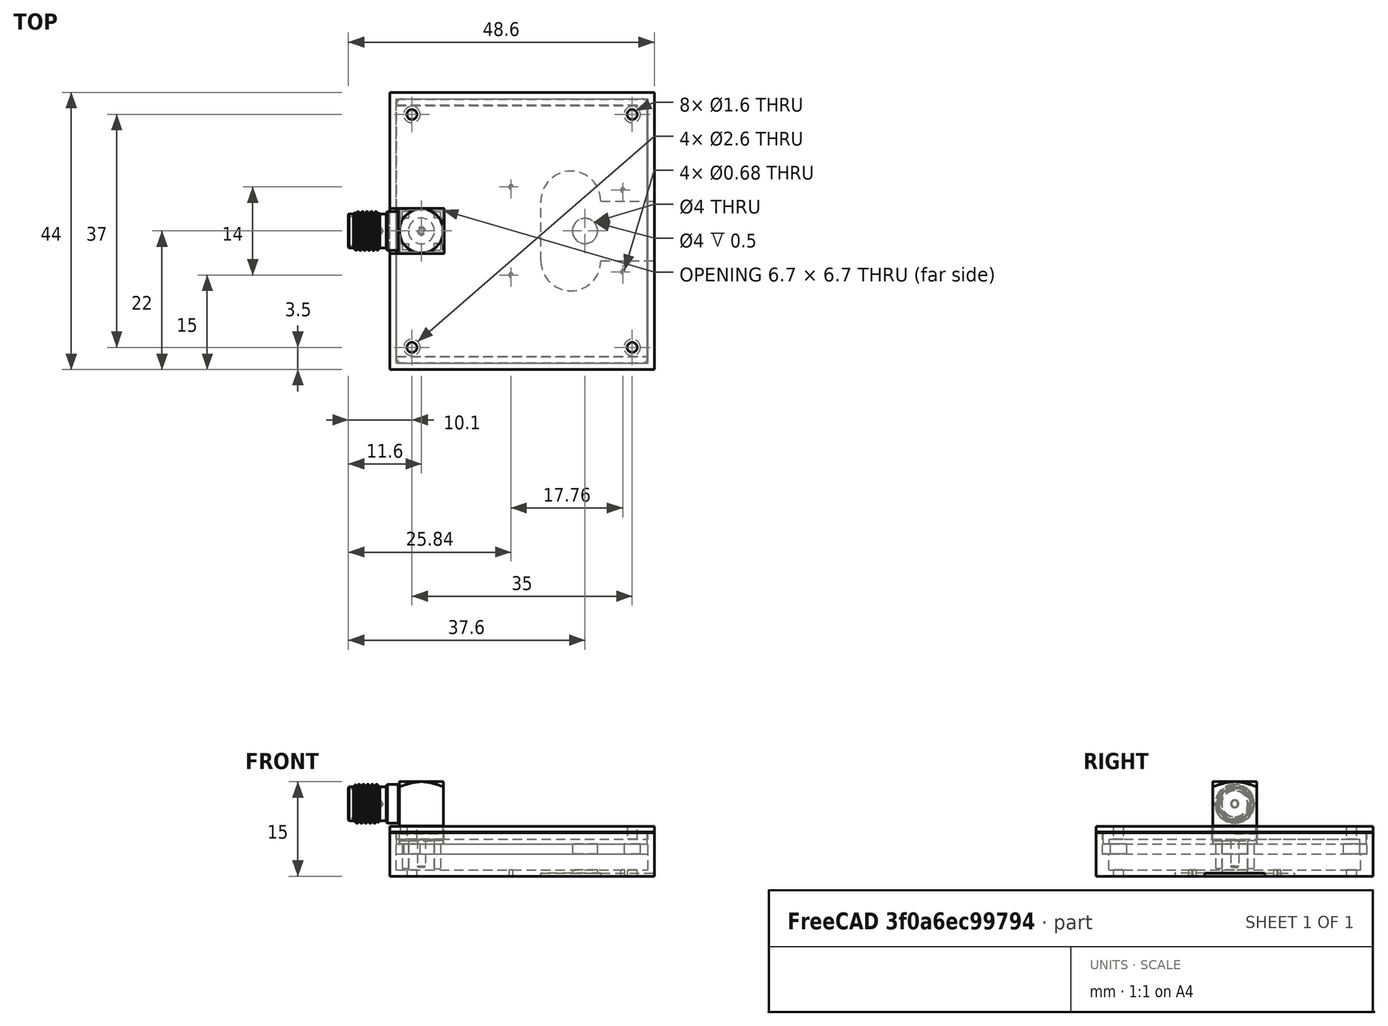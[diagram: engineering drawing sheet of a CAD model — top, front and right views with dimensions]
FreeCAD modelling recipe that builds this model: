
FCSTD DOCUMENT  (FreeCAD 0.20R29603 (Git))
Label: ModulationKickerHousing
License: All rights reserved
LicenseURL: http://en.wikipedia.org/wiki/All_rights_reserved
objects: TechDraw::DrawViewDimension×40, Part::Cylinder×20, Part::Box×11, Part::Cut×9, TechDraw::DrawProjGroupItem×9, Part::Compound×7, Part::MultiFuse×4, TechDraw::DrawSVGTemplate×3, TechDraw::DrawProjGroup×3, TechDraw::DrawPage×3, Part::Feature×1, Part::Fillet×1, TechDraw::DrawViewSection×1
note: 53 computed .brp shape members not serialized (recipe doc carries the construction recipe); baked Part::Feature solids carry a one-line shape summary decoded from their .brp

FEATURE [Part::Box] Box  label="Würfel"
  AttacherType = Attacher::AttachEngine3D
  Height = 1.6
  Length = 40
  Width = 42
FEATURE [Part::Feature] Solid  label="901-143-6RFX"
  Placement = pos=(0,0,0) rot=(1,0,0;-1.5708rad)
  shape: bbox 16.55 x 9.9 x 13.8 mm, 108 faces (baked)
FEATURE [Part::Compound] Compound
  Links = -> [Solid]
  Placement = pos=(4,21,8) rot=(0,0,1;3.14159rad)
FEATURE [Part::Cylinder] Cylinder  label="Zylinder"
  Angle = 360
  AttacherType = Attacher::AttachEngine3D
  FirstAngle = 0
  Height = 5
  Placement = pos=(30,21,0) rot=(0,0,1;0rad)
  Radius = 2
  SecondAngle = 0
FEATURE [Part::Cut] Cut
  Base = -> Box
  Tool = -> Cylinder
FEATURE [Part::Box] Box001  label="Würfel001"
  AttacherType = Attacher::AttachEngine3D
  Height = 7
  Length = 42
  Placement = pos=(-1,-1,-4.4) rot=(0,0,1;0rad)
  Width = 44
FEATURE [Part::Box] Box002  label="Würfel002"
  AttacherType = Attacher::AttachEngine3D
  Height = 6
  Length = 40
  Placement = pos=(0,0,-3.4) rot=(0,0,1;0rad)
  Width = 42
FEATURE [Part::Cut] Cut001
  Base = -> Box001
  Tool = -> Box002
FEATURE [Part::Compound] Compound001  label="PCB"
  Links = -> [Cut,Compound]
  Placement = pos=(0,0,-0.9) rot=(0,0,1;0rad)
FEATURE [Part::Cylinder] Cylinder001  label="Zylinder001"
  Angle = 360
  AttacherType = Attacher::AttachEngine3D
  FirstAngle = 0
  Height = 20
  Placement = pos=(30,21,-10) rot=(0,0,1;0rad)
  Radius = 2
  SecondAngle = 0
FEATURE [Part::Cut] Cut002
  Base = -> Cut001
  Tool = -> Cylinder001
FEATURE [Part::Box] Box003  label="Würfel003"
  AttacherType = Attacher::AttachEngine3D
  Height = 2.5
  Length = 40
  Placement = pos=(0,0,-3.4) rot=(0,0,1;0rad)
  Width = 1
FEATURE [Part::Box] Box004  label="Würfel004"
  AttacherType = Attacher::AttachEngine3D
  Height = 2.5
  Length = 40
  Placement = pos=(0,41,-3.4) rot=(0,0,1;0rad)
  Width = 1
FEATURE [Part::MultiFuse] Fusion
  Shapes = -> [Box003,Box004,Cut002]
FEATURE [Part::Fillet] Fillet  label="PCBRound"
  Base = -> Compound001
  Edges = 4 edges r=1: [Edge1,Edge3,Edge6,Edge12]
FEATURE [Part::Box] Box005  label="Würfel005"
  AttacherType = Attacher::AttachEngine3D
  Height = 1
  Length = 39.8
  Placement = pos=(0.1,0.1,1.5) rot=(0,0,1;0rad)
  Width = 41.8
FEATURE [Part::Box] Box006  label="Würfel006"
  AttacherType = Attacher::AttachEngine3D
  Height = 1
  Length = 42
  Placement = pos=(-1,-1,2.5) rot=(0,0,1;0rad)
  Width = 44
FEATURE [Part::MultiFuse] Fusion001
  Shapes = -> [Box005,Box006]
FEATURE [Part::Box] Box007  label="Würfel007"
  AttacherType = Attacher::AttachEngine3D
  Height = 10
  Length = 20
  Placement = pos=(-12.4,17.4,0) rot=(0,0,1;0rad)
  Width = 7.2
FEATURE [Part::Cut] Cut003
  Base = -> Fusion001
  Tool = -> Box007
FEATURE [Part::Box] Box008  label="Würfel008"
  AttacherType = Attacher::AttachEngine3D
  Height = 0.5
  Length = 18
  Placement = pos=(23,16.25,-4.4) rot=(0,0,1;0rad)
  Width = 9.5
FEATURE [Part::Cylinder] Cylinder002  label="Zylinder002"
  Angle = 360
  AttacherType = Attacher::AttachEngine3D
  FirstAngle = 0
  Height = 0.5
  Placement = pos=(27.75,25.75,-4.4) rot=(0,0,1;0rad)
  Radius = 4.75
  SecondAngle = 0
FEATURE [Part::Cylinder] Cylinder003  label="Zylinder003"
  Angle = 360
  AttacherType = Attacher::AttachEngine3D
  FirstAngle = 0
  Height = 0.5
  Placement = pos=(27.75,16.25,-4.4) rot=(0,0,1;0rad)
  Radius = 4.75
  SecondAngle = 0
FEATURE [Part::MultiFuse] Fusion002
  Shapes = -> [Box008,Cylinder002,Cylinder003]
FEATURE [Part::Cut] Cut004
  Base = -> Fusion
  Tool = -> Fusion002
FEATURE [Part::Cylinder] Cylinder004  label="Zylinder004"
  Angle = 360
  AttacherType = Attacher::AttachEngine3D
  FirstAngle = 0
  Height = 100
  Placement = pos=(18.24,14,-50) rot=(0,0,1;0rad)
  Radius = 0.34
  SecondAngle = 0
FEATURE [Part::Cylinder] Cylinder005  label="Zylinder005"
  Angle = 360
  AttacherType = Attacher::AttachEngine3D
  FirstAngle = 0
  Height = 100
  Placement = pos=(18.24,28,-50) rot=(0,0,1;0rad)
  Radius = 0.34
  SecondAngle = 0
FEATURE [Part::Cylinder] Cylinder006  label="Zylinder006"
  Angle = 360
  AttacherType = Attacher::AttachEngine3D
  FirstAngle = 0
  Height = 100
  Placement = pos=(36,14.5,-50) rot=(0,0,1;0rad)
  Radius = 0.34
  SecondAngle = 0
FEATURE [Part::Cylinder] Cylinder007  label="Zylinder007"
  Angle = 360
  AttacherType = Attacher::AttachEngine3D
  FirstAngle = 0
  Height = 100
  Placement = pos=(36,27.5,-50) rot=(0,0,1;0rad)
  Radius = 0.34
  SecondAngle = 0
FEATURE [Part::Compound] Compound002  label="M1TapHoles"
  Links = -> [Cylinder004,Cylinder005,Cylinder006,Cylinder007]
FEATURE [Part::Cut] Cut005
  Base = -> Cut004
  Tool = -> Compound002
FEATURE [Part::Box] Box009  label="Würfel009"
  AttacherType = Attacher::AttachEngine3D
  Height = 0.8
  Length = 39.8
  Placement = pos=(0.1,40.9,0.7) rot=(0,0,1;0rad)
  Width = 1
FEATURE [Part::Box] Box010  label="Würfel010"
  AttacherType = Attacher::AttachEngine3D
  Height = 0.8
  Length = 39.8
  Placement = pos=(0.1,0.1,0.7) rot=(0,0,1;0rad)
  Width = 1
FEATURE [Part::Compound] Compound003
  Links = -> [Box009,Box010]
FEATURE [Part::MultiFuse] Fusion003
  Shapes = -> [Cut003,Compound003]
FEATURE [Part::Cylinder] Cylinder008  label="Zylinder008"
  Angle = 360
  AttacherType = Attacher::AttachEngine3D
  FirstAngle = 0
  Height = 20
  Placement = pos=(37.5,2.5,-10) rot=(0,0,1;0rad)
  Radius = 0.8
  SecondAngle = 0
FEATURE [Part::Cylinder] Cylinder009  label="Zylinder009"
  Angle = 360
  AttacherType = Attacher::AttachEngine3D
  FirstAngle = 0
  Height = 20
  Placement = pos=(2.5,2.5,-10) rot=(0,0,1;0rad)
  Radius = 0.8
  SecondAngle = 0
FEATURE [Part::Cylinder] Cylinder010  label="Zylinder010"
  Angle = 360
  AttacherType = Attacher::AttachEngine3D
  FirstAngle = 0
  Height = 20
  Placement = pos=(37.5,39.5,-10) rot=(0,0,1;0rad)
  Radius = 0.8
  SecondAngle = 0
FEATURE [Part::Cylinder] Cylinder011  label="Zylinder011"
  Angle = 360
  AttacherType = Attacher::AttachEngine3D
  FirstAngle = 0
  Height = 20
  Placement = pos=(2.5,39.5,-10) rot=(0,0,1;0rad)
  Radius = 0.8
  SecondAngle = 0
FEATURE [Part::Cylinder] Cylinder012  label="Zylinder012"
  Angle = 360
  AttacherType = Attacher::AttachEngine3D
  FirstAngle = 0
  Height = 20
  Placement = pos=(37.5,2.5,-10) rot=(0,0,1;0rad)
  Radius = 1.3
  SecondAngle = 0
FEATURE [Part::Cylinder] Cylinder013  label="Zylinder013"
  Angle = 360
  AttacherType = Attacher::AttachEngine3D
  FirstAngle = 0
  Height = 20
  Placement = pos=(2.5,2.5,-10) rot=(0,0,1;0rad)
  Radius = 1.3
  SecondAngle = 0
FEATURE [Part::Cylinder] Cylinder014  label="Zylinder014"
  Angle = 360
  AttacherType = Attacher::AttachEngine3D
  FirstAngle = 0
  Height = 20
  Placement = pos=(37.5,39.5,-10) rot=(0,0,1;0rad)
  Radius = 1.3
  SecondAngle = 0
FEATURE [Part::Cylinder] Cylinder015  label="Zylinder015"
  Angle = 360
  AttacherType = Attacher::AttachEngine3D
  FirstAngle = 0
  Height = 20
  Placement = pos=(2.5,39.5,-10) rot=(0,0,1;0rad)
  Radius = 1.3
  SecondAngle = 0
FEATURE [Part::Compound] Compound004
  Links = -> [Cylinder015,Cylinder012,Cylinder013,Cylinder014]
FEATURE [Part::Cut] Cut006  label="PCBWithHoles"
  Base = -> Fillet
  Tool = -> Compound004
FEATURE [Part::Cylinder] Cylinder016  label="Zylinder016"
  Angle = 360
  AttacherType = Attacher::AttachEngine3D
  FirstAngle = 0
  Height = 20
  Placement = pos=(37.5,2.5,-10) rot=(0,0,1;0rad)
  Radius = 0.8
  SecondAngle = 0
FEATURE [Part::Cylinder] Cylinder017  label="Zylinder017"
  Angle = 360
  AttacherType = Attacher::AttachEngine3D
  FirstAngle = 0
  Height = 20
  Placement = pos=(2.5,2.5,-10) rot=(0,0,1;0rad)
  Radius = 0.8
  SecondAngle = 0
FEATURE [Part::Cylinder] Cylinder018  label="Zylinder018"
  Angle = 360
  AttacherType = Attacher::AttachEngine3D
  FirstAngle = 0
  Height = 20
  Placement = pos=(37.5,39.5,-10) rot=(0,0,1;0rad)
  Radius = 0.8
  SecondAngle = 0
FEATURE [Part::Cylinder] Cylinder019  label="Zylinder019"
  Angle = 360
  AttacherType = Attacher::AttachEngine3D
  FirstAngle = 0
  Height = 20
  Placement = pos=(2.5,39.5,-10) rot=(0,0,1;0rad)
  Radius = 0.8
  SecondAngle = 0
FEATURE [Part::Compound] Compound005
  Links = -> [Cylinder008,Cylinder009,Cylinder010,Cylinder011]
FEATURE [Part::Cut] Cut007  label="UpperPart"
  Base = -> Cut005
  Tool = -> Compound005
FEATURE [TechDraw::DrawSVGTemplate] Template
  EditableTexts = Designed_by_Name=Thomas Spielauer; FC-Date=2023-07-14; FC-SC=mm; FC-SH=1/1; FC-Title=eBeam Deflector; Subtitle=Lower Part
  Height = 210
  Orientation = 1
  Width = 297
FEATURE [Part::Compound] Compound006
  Links = -> [Cylinder019,Cylinder016,Cylinder017,Cylinder018]
FEATURE [Part::Cut] Cut008  label="LowerPart"
  Base = -> Fusion003
  Tool = -> Compound006
FEATURE [TechDraw::DrawProjGroupItem] ProjItem  label="Front"
  CoarseView = false
  Direction = (0,0,1)
  Focus = 100
  HardHidden = false
  IsoCount = 0
  IsoHidden = false
  IsoVisible = false
  LockPosition = true
  Perspective = false
  Rotation = 0
  RotationVector = (0,-1,0)
  Scale = 2
  ScaleType = 2
  SeamHidden = false
  SeamVisible = true
  SmoothHidden = false
  SmoothVisible = true
  Source = -> [Cut008]
  Type = 0
  X = 0
  XDirection = (0,-1,0)
  Y = 0
FEATURE [TechDraw::DrawProjGroupItem] ProjItem001  label="Right"
  CoarseView = false
  Direction = (0,-1,1e-16)
  Focus = 100
  HardHidden = false
  IsoCount = 0
  IsoHidden = false
  IsoVisible = false
  LockPosition = false
  Perspective = false
  Rotation = 0
  RotationVector = (1,0,0)
  Scale = 2
  ScaleType = 2
  SeamHidden = false
  SeamVisible = true
  SmoothHidden = false
  SmoothVisible = true
  Source = -> [Cut008]
  Type = 2
  X = -102.572
  XDirection = (0,-1e-16,-1)
  Y = 0
FEATURE [TechDraw::DrawProjGroupItem] ProjItem002  label="Left"
  CoarseView = false
  Direction = (0,1,1e-16)
  Focus = 100
  HardHidden = false
  IsoCount = 0
  IsoHidden = false
  IsoVisible = false
  LockPosition = false
  Perspective = false
  Rotation = 0
  RotationVector = (1,0,0)
  Scale = 2
  ScaleType = 2
  SeamHidden = false
  SeamVisible = true
  SmoothHidden = false
  SmoothVisible = true
  Source = -> [Cut008]
  Type = 1
  X = 96.1545
  XDirection = (0,-1e-16,1)
  Y = 0
FEATURE [TechDraw::DrawProjGroupItem] ProjItem003  label="Bottom"
  CoarseView = false
  Direction = (-1,0,0)
  Focus = 100
  HardHidden = false
  IsoCount = 0
  IsoHidden = false
  IsoVisible = false
  LockPosition = false
  Perspective = false
  Rotation = 0
  RotationVector = (1,0,0)
  Scale = 2
  ScaleType = 2
  SeamHidden = false
  SeamVisible = true
  SmoothHidden = false
  SmoothVisible = true
  Source = -> [Cut008]
  Type = 5
  X = 0
  XDirection = (0,-1,0)
  Y = 72.4737
FEATURE [TechDraw::DrawProjGroup] ProjGroup
  Anchor = -> ProjItem
  AutoDistribute = false
  LockPosition = false
  ProjectionType = 0
  Rotation = 0
  Scale = 2
  ScaleType = 2
  Source = -> [Cut008]
  Views = -> [ProjItem,ProjItem001,ProjItem002,ProjItem003]
  X = 141.227
  Y = 109.706
  spacingX = 15
  spacingY = 15
FEATURE [TechDraw::DrawViewDimension] Dimension
  AngleOverride = false
  Arbitrary = false
  ArbitraryTolerances = false
  EqualTolerance = true
  ExtensionAngle = 0
  FormatSpec = %.2w
  FormatSpecOverTolerance = %+.2w
  FormatSpecUnderTolerance = %+.2w
  Inverted = false
  LineAngle = 0
  LockPosition = false
  MeasureType = 1
  OverTolerance = 0
  References2D = -> [ProjItem]
  Rotation = 0
  ScaleType = 0
  TheoreticalExact = false
  Type = 0
  UnderTolerance = 0
  X = 1.03164
  Y = 52.3405
FEATURE [TechDraw::DrawViewDimension] Dimension001
  AngleOverride = false
  Arbitrary = false
  ArbitraryTolerances = false
  EqualTolerance = true
  ExtensionAngle = 0
  FormatSpec = %.2w
  FormatSpecOverTolerance = %+.2w
  FormatSpecUnderTolerance = %+.2w
  Inverted = false
  LineAngle = 0
  LockPosition = false
  MeasureType = 1
  OverTolerance = 0
  References2D = -> [ProjItem]
  Rotation = 0
  ScaleType = 0
  TheoreticalExact = false
  Type = 0
  UnderTolerance = 0
  X = 50.3286
  Y = 2.95204
FEATURE [TechDraw::DrawViewDimension] Dimension002
  AngleOverride = false
  Arbitrary = false
  ArbitraryTolerances = false
  EqualTolerance = true
  ExtensionAngle = 0
  FormatSpec = %.2w
  FormatSpecOverTolerance = %+.2w
  FormatSpecUnderTolerance = %+.2w
  Inverted = false
  LineAngle = 0
  LockPosition = false
  MeasureType = 1
  OverTolerance = 0
  References2D = -> [ProjItem]
  Rotation = 0
  ScaleType = 0
  TheoreticalExact = false
  Type = 0
  UnderTolerance = 0
  X = 25.826
  Y = -44.2465
FEATURE [TechDraw::DrawViewDimension] Dimension003
  AngleOverride = false
  Arbitrary = false
  ArbitraryTolerances = false
  EqualTolerance = true
  ExtensionAngle = 0
  FormatSpec = %.2w
  FormatSpecOverTolerance = %+.2w
  FormatSpecUnderTolerance = %+.2w
  Inverted = false
  LineAngle = 0
  LockPosition = false
  MeasureType = 1
  OverTolerance = 0
  References2D = -> [ProjItem]
  Rotation = 0
  ScaleType = 0
  TheoreticalExact = false
  Type = 0
  UnderTolerance = 0
  X = 0
  Y = -43.9981
FEATURE [TechDraw::DrawViewDimension] Dimension004
  AngleOverride = false
  Arbitrary = false
  ArbitraryTolerances = false
  EqualTolerance = true
  ExtensionAngle = 0
  FormatSpec = ⌀%.2w (M2 Senkkopf 4x)
  FormatSpecOverTolerance = %+.2w
  FormatSpecUnderTolerance = %+.2w
  Inverted = false
  LineAngle = 0
  LockPosition = false
  MeasureType = 1
  OverTolerance = 0
  References2D = -> [ProjItem]
  Rotation = 0
  ScaleType = 0
  TheoreticalExact = false
  Type = 5
  UnderTolerance = 0
  X = -15.26
  Y = -16.466
FEATURE [TechDraw::DrawViewDimension] Dimension005
  AngleOverride = false
  Arbitrary = false
  ArbitraryTolerances = false
  EqualTolerance = true
  ExtensionAngle = 0
  FormatSpec = %.2w
  FormatSpecOverTolerance = %+.2w
  FormatSpecUnderTolerance = %+.2w
  Inverted = false
  LineAngle = 0
  LockPosition = false
  MeasureType = 1
  OverTolerance = 0
  References2D = -> [ProjItem]
  Rotation = 0
  ScaleType = 0
  TheoreticalExact = false
  Type = 0
  UnderTolerance = 0
  X = 17.8136
  Y = -30.4854
FEATURE [TechDraw::DrawViewDimension] Dimension006
  AngleOverride = false
  Arbitrary = false
  ArbitraryTolerances = false
  EqualTolerance = true
  ExtensionAngle = 0
  FormatSpec = %.2w
  FormatSpecOverTolerance = %+.2w
  FormatSpecUnderTolerance = %+.2w
  Inverted = false
  LineAngle = 0
  LockPosition = false
  MeasureType = 1
  OverTolerance = 0
  References2D = -> [ProjItem]
  Rotation = 0
  ScaleType = 0
  TheoreticalExact = false
  Type = 0
  UnderTolerance = 0
  X = 24.0419
  Y = 30.8549
FEATURE [TechDraw::DrawViewDimension] Dimension007
  AngleOverride = false
  Arbitrary = false
  ArbitraryTolerances = false
  EqualTolerance = true
  ExtensionAngle = 0
  FormatSpec = %.2w
  FormatSpecOverTolerance = %+.2w
  FormatSpecUnderTolerance = %+.2w
  Inverted = false
  LineAngle = 0
  LockPosition = false
  MeasureType = 1
  OverTolerance = 0
  References2D = -> [ProjItem]
  Rotation = 0
  ScaleType = 0
  TheoreticalExact = false
  Type = 0
  UnderTolerance = 0
  X = 40.2697
  Y = 27.0498
FEATURE [TechDraw::DrawViewDimension] Dimension009
  AngleOverride = false
  Arbitrary = false
  ArbitraryTolerances = false
  EqualTolerance = true
  ExtensionAngle = 0
  FormatSpec = %.2w
  FormatSpecOverTolerance = %+.2w
  FormatSpecUnderTolerance = %+.2w
  Inverted = false
  LineAngle = 0
  LockPosition = false
  MeasureType = 1
  OverTolerance = 0
  References2D = -> [ProjItem001]
  Rotation = 0
  ScaleType = 0
  TheoreticalExact = false
  Type = 0
  UnderTolerance = 0
  X = -13.7258
  Y = 67.2052
FEATURE [TechDraw::DrawViewDimension] Dimension010
  AngleOverride = false
  Arbitrary = false
  ArbitraryTolerances = false
  EqualTolerance = true
  ExtensionAngle = 0
  FormatSpec = %.2w
  FormatSpecOverTolerance = %+.2w
  FormatSpecUnderTolerance = %+.2w
  Inverted = false
  LineAngle = 0
  LockPosition = false
  MeasureType = 1
  OverTolerance = 0
  References2D = -> [ProjItem001]
  Rotation = 0
  ScaleType = 0
  TheoreticalExact = false
  Type = 0
  UnderTolerance = 0
  X = -13.5281
  Y = 59.8272
FEATURE [TechDraw::DrawViewDimension] Dimension011
  AngleOverride = false
  Arbitrary = false
  ArbitraryTolerances = false
  EqualTolerance = true
  ExtensionAngle = 0
  FormatSpec = %.2w
  FormatSpecOverTolerance = %+.2w
  FormatSpecUnderTolerance = %+.2w
  Inverted = false
  LineAngle = 0
  LockPosition = false
  MeasureType = 1
  OverTolerance = 0
  References2D = -> [ProjItem001]
  Rotation = 0
  ScaleType = 0
  TheoreticalExact = false
  Type = 0
  UnderTolerance = 0
  X = -11.7281
  Y = 52.764
FEATURE [TechDraw::DrawViewDimension] Dimension012
  AngleOverride = false
  Arbitrary = false
  ArbitraryTolerances = false
  EqualTolerance = true
  ExtensionAngle = 0
  FormatSpec = %.2w
  FormatSpecOverTolerance = %+.2w
  FormatSpecUnderTolerance = %+.2w
  Inverted = false
  LineAngle = 0
  LockPosition = false
  MeasureType = 1
  OverTolerance = 0
  References2D = -> [ProjItem001]
  Rotation = 0
  ScaleType = 0
  TheoreticalExact = false
  Type = 0
  UnderTolerance = 0
  X = 10.0894
  Y = -0.126874
FEATURE [TechDraw::DrawViewDimension] Dimension013
  AngleOverride = false
  Arbitrary = false
  ArbitraryTolerances = false
  EqualTolerance = true
  ExtensionAngle = 0
  FormatSpec = %.2w
  FormatSpecOverTolerance = %+.2w
  FormatSpecUnderTolerance = %+.2w
  Inverted = false
  LineAngle = 0
  LockPosition = false
  MeasureType = 1
  OverTolerance = 0
  References2D = -> [ProjItem001]
  Rotation = 0
  ScaleType = 0
  TheoreticalExact = false
  Type = 0
  UnderTolerance = 0
  X = 27.8811
  Y = -46.6822
FEATURE [TechDraw::DrawViewDimension] Dimension014
  AngleOverride = false
  Arbitrary = false
  ArbitraryTolerances = false
  EqualTolerance = true
  ExtensionAngle = 0
  FormatSpec = %.2w
  FormatSpecOverTolerance = %+.2w
  FormatSpecUnderTolerance = %+.2w
  Inverted = false
  LineAngle = 0
  LockPosition = false
  MeasureType = 1
  OverTolerance = 0
  References2D = -> [ProjItem001]
  Rotation = 0
  ScaleType = 0
  TheoreticalExact = false
  Type = 0
  UnderTolerance = 0
  X = 18.5153
  Y = 49.0826
FEATURE [TechDraw::DrawViewDimension] Dimension015
  AngleOverride = false
  Arbitrary = false
  ArbitraryTolerances = false
  EqualTolerance = true
  ExtensionAngle = 0
  FormatSpec = %.2w
  FormatSpecOverTolerance = %+.2w
  FormatSpecUnderTolerance = %+.2w
  Inverted = false
  LineAngle = 0
  LockPosition = false
  MeasureType = 1
  OverTolerance = 0
  References2D = -> [ProjItem003]
  Rotation = 0
  ScaleType = 0
  TheoreticalExact = false
  Type = 0
  UnderTolerance = 0
  X = -46.397
  Y = -5.97196
FEATURE [TechDraw::DrawViewDimension] Dimension016
  AngleOverride = false
  Arbitrary = false
  ArbitraryTolerances = false
  EqualTolerance = true
  ExtensionAngle = 0
  FormatSpec = %.2w
  FormatSpecOverTolerance = %+.2w
  FormatSpecUnderTolerance = %+.2w
  Inverted = false
  LineAngle = 0
  LockPosition = false
  MeasureType = 1
  OverTolerance = 0
  References2D = -> [ProjItem003]
  Rotation = 0
  ScaleType = 0
  TheoreticalExact = false
  Type = 0
  UnderTolerance = 0
  X = -51.4683
  Y = 13.8663
FEATURE [TechDraw::DrawPage] Page
  KeepUpdated = true
  NextBalloonIndex = 1
  ProjectionType = 0
  Template = -> Template
  Views = -> [ProjGroup,Dimension,Dimension001,Dimension002,Dimension003,Dimension004,Dimension005,Dimension006,Dimension007,Dimension009,Dimension010,Dimension011,Dimension012,Dimension013,Dimension014,Dimension015,Dimension016]
FEATURE [TechDraw::DrawSVGTemplate] Template001
  EditableTexts = Designed_by_Name=Thomas Spielauer; FC-Date=2023-07-14; FC-SC=mm; FC-SH=1/2; FC-Title=eBeam Deflector; Subtitle=Upper Part
  Height = 210
  Orientation = 1
  Width = 297
FEATURE [TechDraw::DrawProjGroupItem] ProjItem004  label="Front001"
  CoarseView = false
  Direction = (0,0,-1)
  Focus = 100
  HardHidden = false
  IsoCount = 0
  IsoHidden = false
  IsoVisible = false
  LockPosition = true
  Perspective = false
  Rotation = 0
  RotationVector = (-1,0,0)
  Scale = 2
  ScaleType = 2
  SeamHidden = false
  SeamVisible = true
  SmoothHidden = false
  SmoothVisible = true
  Source = -> [Cut007]
  Type = 0
  X = 0
  XDirection = (-1,0,0)
  Y = 0
FEATURE [TechDraw::DrawProjGroupItem] ProjItem005  label="Right001"
  CoarseView = false
  Direction = (-1,0,-1e-16)
  Focus = 100
  HardHidden = false
  IsoCount = 0
  IsoHidden = false
  IsoVisible = false
  LockPosition = false
  Perspective = false
  Rotation = 0
  RotationVector = (1,0,0)
  Scale = 2
  ScaleType = 2
  SeamHidden = false
  SeamVisible = true
  SmoothHidden = false
  SmoothVisible = true
  Source = -> [Cut007]
  Type = 2
  X = -99
  XDirection = (-1e-16,0,1)
  Y = 0
FEATURE [TechDraw::DrawProjGroupItem] ProjItem006  label="Left001"
  CoarseView = false
  Direction = (1,0,-1e-16)
  Focus = 100
  HardHidden = false
  IsoCount = 0
  IsoHidden = false
  IsoVisible = false
  LockPosition = false
  Perspective = false
  Rotation = 0
  RotationVector = (1,0,0)
  Scale = 2
  ScaleType = 2
  SeamHidden = false
  SeamVisible = true
  SmoothHidden = false
  SmoothVisible = true
  Source = -> [Cut007]
  Type = 1
  X = 99
  XDirection = (-1e-16,0,-1)
  Y = 0
FEATURE [TechDraw::DrawProjGroupItem] ProjItem007  label="Bottom001"
  CoarseView = false
  Direction = (0,-1,0)
  Focus = 100
  HardHidden = false
  IsoCount = 0
  IsoHidden = false
  IsoVisible = false
  LockPosition = false
  Perspective = false
  Rotation = 0
  RotationVector = (1,0,0)
  Scale = 2
  ScaleType = 2
  SeamHidden = false
  SeamVisible = true
  SmoothHidden = false
  SmoothVisible = true
  Source = -> [Cut007]
  Type = 5
  X = 0
  XDirection = (-1,0,0)
  Y = 103
FEATURE [TechDraw::DrawProjGroup] ProjGroup001
  Anchor = -> ProjItem004
  AutoDistribute = true
  LockPosition = false
  ProjectionType = 0
  Rotation = 0
  Scale = 2
  ScaleType = 2
  Source = -> [Cut007]
  Views = -> [ProjItem004,ProjItem005,ProjItem006,ProjItem007]
  X = 146.832
  Y = 117.067
  spacingX = 15
  spacingY = 15
FEATURE [TechDraw::DrawViewDimension] Dimension017
  AngleOverride = false
  Arbitrary = false
  ArbitraryTolerances = false
  EqualTolerance = true
  ExtensionAngle = 0
  FormatSpec = %.2w
  FormatSpecOverTolerance = %+.2w
  FormatSpecUnderTolerance = %+.2w
  Inverted = false
  LineAngle = 0
  LockPosition = false
  MeasureType = 1
  OverTolerance = 0
  References2D = -> [ProjItem005]
  Rotation = 0
  ScaleType = 0
  TheoreticalExact = false
  Type = 0
  UnderTolerance = 0
  X = 19.3978
  Y = 2.5
FEATURE [TechDraw::DrawViewDimension] Dimension018
  AngleOverride = false
  Arbitrary = false
  ArbitraryTolerances = false
  EqualTolerance = true
  ExtensionAngle = 0
  FormatSpec = %.2w
  FormatSpecOverTolerance = %+.2w
  FormatSpecUnderTolerance = %+.2w
  Inverted = false
  LineAngle = 0
  LockPosition = false
  MeasureType = 1
  OverTolerance = 0
  References2D = -> [ProjItem005]
  Rotation = 0
  ScaleType = 0
  TheoreticalExact = false
  Type = 0
  UnderTolerance = 0
  X = 0.029867
  Y = 58.5425
FEATURE [TechDraw::DrawViewDimension] Dimension019
  AngleOverride = false
  Arbitrary = false
  ArbitraryTolerances = false
  EqualTolerance = true
  ExtensionAngle = 0
  FormatSpec = %.2w
  FormatSpecOverTolerance = %+.2w
  FormatSpecUnderTolerance = %+.2w
  Inverted = false
  LineAngle = 0
  LockPosition = false
  MeasureType = 1
  OverTolerance = 0
  References2D = -> [ProjItem007]
  Rotation = 0
  ScaleType = 0
  TheoreticalExact = false
  Type = 0
  UnderTolerance = 0
  X = 0.976415
  Y = 16.305
FEATURE [TechDraw::DrawViewDimension] Dimension020
  AngleOverride = false
  Arbitrary = false
  ArbitraryTolerances = false
  EqualTolerance = true
  ExtensionAngle = 0
  FormatSpec = %.2w
  FormatSpecOverTolerance = %+.2w
  FormatSpecUnderTolerance = %+.2w
  Inverted = false
  LineAngle = 0
  LockPosition = false
  MeasureType = 1
  OverTolerance = 0
  References2D = -> [ProjItem007]
  Rotation = 0
  ScaleType = 0
  TheoreticalExact = false
  Type = 0
  UnderTolerance = 0
  X = 56.9717
  Y = 3.12108
FEATURE [TechDraw::DrawViewDimension] Dimension021
  AngleOverride = false
  Arbitrary = false
  ArbitraryTolerances = false
  EqualTolerance = true
  ExtensionAngle = 0
  FormatSpec = %.2w
  FormatSpecOverTolerance = %+.2w
  FormatSpecUnderTolerance = %+.2w
  Inverted = false
  LineAngle = 0
  LockPosition = false
  MeasureType = 1
  OverTolerance = 0
  References2D = -> [ProjItem004]
  Rotation = 0
  ScaleType = 0
  TheoreticalExact = false
  Type = 0
  UnderTolerance = 0
  X = -35.9872
  Y = 1.87216
FEATURE [TechDraw::DrawViewDimension] Dimension022
  AngleOverride = false
  Arbitrary = false
  ArbitraryTolerances = false
  EqualTolerance = true
  ExtensionAngle = 0
  FormatSpec = R%.2w
  FormatSpecOverTolerance = %+.2w
  FormatSpecUnderTolerance = %+.2w
  Inverted = false
  LineAngle = 0
  LockPosition = false
  MeasureType = 1
  OverTolerance = 0
  References2D = -> [ProjItem004]
  Rotation = 0
  ScaleType = 0
  TheoreticalExact = false
  Type = 4
  UnderTolerance = 0
  X = -6.03394
  Y = -23.6789
FEATURE [TechDraw::DrawViewDimension] Dimension023
  AngleOverride = false
  Arbitrary = false
  ArbitraryTolerances = false
  EqualTolerance = true
  ExtensionAngle = 0
  FormatSpec = R%.2w
  FormatSpecOverTolerance = %+.2w
  FormatSpecUnderTolerance = %+.2w
  Inverted = false
  LineAngle = 0
  LockPosition = false
  MeasureType = 1
  OverTolerance = 0
  References2D = -> [ProjItem004]
  Rotation = 0
  ScaleType = 0
  TheoreticalExact = false
  Type = 4
  UnderTolerance = 0
  X = -12.1225
  Y = 29.1971
FEATURE [TechDraw::DrawViewDimension] Dimension024
  AngleOverride = false
  Arbitrary = false
  ArbitraryTolerances = false
  EqualTolerance = true
  ExtensionAngle = 0
  FormatSpec = %.2w
  FormatSpecOverTolerance = %+.2w
  FormatSpecUnderTolerance = %+.2w
  Inverted = false
  LineAngle = 0
  LockPosition = false
  MeasureType = 1
  OverTolerance = 0
  References2D = -> [ProjItem004]
  Rotation = 0
  ScaleType = 0
  TheoreticalExact = false
  Type = 0
  UnderTolerance = 0
  X = 38.5
  Y = -23.9278
FEATURE [TechDraw::DrawViewDimension] Dimension025
  AngleOverride = false
  Arbitrary = false
  ArbitraryTolerances = false
  EqualTolerance = true
  ExtensionAngle = 0
  FormatSpec = %.2w
  FormatSpecOverTolerance = %+.2w
  FormatSpecUnderTolerance = %+.2w
  Inverted = false
  LineAngle = 0
  LockPosition = false
  MeasureType = 1
  OverTolerance = 0
  References2D = -> [ProjItem004]
  Rotation = 0
  ScaleType = 0
  TheoreticalExact = false
  Type = 0
  UnderTolerance = 0
  X = 29.4448
  Y = -37.8248
FEATURE [TechDraw::DrawViewDimension] Dimension026
  AngleOverride = false
  Arbitrary = false
  ArbitraryTolerances = false
  EqualTolerance = true
  ExtensionAngle = 0
  FormatSpec = ⌀%.2w (M2, tapped)
  FormatSpecOverTolerance = %+.2w
  FormatSpecUnderTolerance = %+.2w
  Inverted = false
  LineAngle = 0
  LockPosition = false
  MeasureType = 1
  OverTolerance = 0
  References2D = -> [ProjItem004]
  Rotation = 0
  ScaleType = 0
  TheoreticalExact = false
  Type = 5
  UnderTolerance = 0
  X = 55.6626
  Y = 58.789
FEATURE [TechDraw::DrawViewDimension] Dimension027
  AngleOverride = false
  Arbitrary = false
  ArbitraryTolerances = false
  EqualTolerance = true
  ExtensionAngle = 0
  FormatSpec = %.2w
  FormatSpecOverTolerance = %+.2w
  FormatSpecUnderTolerance = %+.2w
  Inverted = false
  LineAngle = 0
  LockPosition = false
  MeasureType = 1
  OverTolerance = 0
  References2D = -> [ProjItem004]
  Rotation = 0
  ScaleType = 0
  TheoreticalExact = false
  Type = 0
  UnderTolerance = 0
  X = 61.7769
  Y = 24.657
FEATURE [TechDraw::DrawViewDimension] Dimension028
  AngleOverride = false
  Arbitrary = false
  ArbitraryTolerances = false
  EqualTolerance = true
  ExtensionAngle = 0
  FormatSpec = ⌀%.2w (M1, 4x)
  FormatSpecOverTolerance = %+.2w
  FormatSpecUnderTolerance = %+.2w
  Inverted = false
  LineAngle = 0
  LockPosition = false
  MeasureType = 1
  OverTolerance = 0
  References2D = -> [ProjItem004]
  Rotation = 0
  ScaleType = 0
  TheoreticalExact = false
  Type = 5
  UnderTolerance = 0
  X = 20.165
  Y = -8.29098
FEATURE [TechDraw::DrawViewDimension] Dimension033
  AngleOverride = false
  Arbitrary = false
  ArbitraryTolerances = false
  EqualTolerance = true
  ExtensionAngle = 0
  FormatSpec = ⌀%.2w
  FormatSpecOverTolerance = %+.2w
  FormatSpecUnderTolerance = %+.2w
  Inverted = false
  LineAngle = 0
  LockPosition = false
  MeasureType = 1
  OverTolerance = 0
  References2D = -> [ProjItem004]
  Rotation = 0
  ScaleType = 0
  TheoreticalExact = false
  Type = 5
  UnderTolerance = 0
  X = -10.3584
  Y = -1.4385
FEATURE [TechDraw::DrawViewDimension] Dimension034
  AngleOverride = false
  Arbitrary = false
  ArbitraryTolerances = false
  EqualTolerance = true
  ExtensionAngle = 0
  FormatSpec = %.2w
  FormatSpecOverTolerance = %+.2w
  FormatSpecUnderTolerance = %+.2w
  Inverted = false
  LineAngle = 0
  LockPosition = false
  MeasureType = 1
  OverTolerance = 0
  References2D = -> [ProjItem004]
  Rotation = 0
  ScaleType = 0
  TheoreticalExact = false
  Type = 0
  UnderTolerance = 0
  X = -58.538
  Y = 8.69722
FEATURE [TechDraw::DrawViewDimension] Dimension035
  AngleOverride = false
  Arbitrary = false
  ArbitraryTolerances = false
  EqualTolerance = true
  ExtensionAngle = 0
  FormatSpec = %.2w
  FormatSpecOverTolerance = %+.2w
  FormatSpecUnderTolerance = %+.2w
  Inverted = false
  LineAngle = 0
  LockPosition = false
  MeasureType = 1
  OverTolerance = 0
  References2D = -> [ProjItem004]
  Rotation = 0
  ScaleType = 0
  TheoreticalExact = false
  Type = 0
  UnderTolerance = 0
  X = -48.884
  Y = 26.2793
FEATURE [TechDraw::DrawViewDimension] Dimension036
  AngleOverride = false
  Arbitrary = false
  ArbitraryTolerances = false
  EqualTolerance = true
  ExtensionAngle = 0
  FormatSpec = %.2w
  FormatSpecOverTolerance = %+.2w
  FormatSpecUnderTolerance = %+.2w
  Inverted = false
  LineAngle = 0
  LockPosition = false
  MeasureType = 1
  OverTolerance = 0
  References2D = -> [ProjItem004]
  Rotation = 0
  ScaleType = 0
  TheoreticalExact = false
  Type = 0
  UnderTolerance = 0
  X = -31.4709
  Y = -20.5376
FEATURE [TechDraw::DrawViewDimension] Dimension037
  AngleOverride = false
  Arbitrary = false
  ArbitraryTolerances = false
  EqualTolerance = true
  ExtensionAngle = 0
  FormatSpec = %.2w
  FormatSpecOverTolerance = %+.2w
  FormatSpecUnderTolerance = %+.2w
  Inverted = false
  LineAngle = 0
  LockPosition = false
  MeasureType = 1
  OverTolerance = 0
  References2D = -> [ProjItem004]
  Rotation = 0
  ScaleType = 0
  TheoreticalExact = false
  Type = 0
  UnderTolerance = 0
  X = 22.308
  Y = 26.1867
FEATURE [TechDraw::DrawPage] Page001
  KeepUpdated = true
  NextBalloonIndex = 1
  ProjectionType = 0
  Template = -> Template001
  Views = -> [ProjGroup001,Dimension017,Dimension018,Dimension019,Dimension020,Dimension021,Dimension022,Dimension023,Dimension024,Dimension025,Dimension026,Dimension027,Dimension028,Dimension033,Dimension034,Dimension035,Dimension036,Dimension037]
FEATURE [TechDraw::DrawSVGTemplate] Template002
  EditableTexts = Designed_by_Name=Thomas Spielauer; FC-Date=2023-07-14; FC-SC=mm; FC-SH=2/2; FC-Title=eBeam Deflector; Subtitle=Upper Part
  Height = 210
  Orientation = 1
  Width = 297
FEATURE [TechDraw::DrawProjGroupItem] ProjItem008  label="Front002"
  CoarseView = false
  Direction = (0,0,-1)
  Focus = 100
  HardHidden = false
  IsoCount = 0
  IsoHidden = false
  IsoVisible = false
  LockPosition = true
  Perspective = false
  Rotation = 0
  RotationVector = (-1,0,0)
  Scale = 2
  ScaleType = 2
  SeamHidden = false
  SeamVisible = true
  SmoothHidden = false
  SmoothVisible = true
  Source = -> [Cut007]
  Type = 0
  X = 0
  XDirection = (2e-16,1,0)
  Y = 0
FEATURE [TechDraw::DrawProjGroup] ProjGroup002
  Anchor = -> ProjItem008
  AutoDistribute = true
  LockPosition = false
  ProjectionType = 0
  Rotation = 0
  Scale = 2
  ScaleType = 2
  Source = -> [Cut007]
  Views = -> [ProjItem008]
  X = 68.2793
  Y = 153.846
  spacingX = 15
  spacingY = 15
FEATURE [TechDraw::DrawViewSection] SectionView  label="Section  - "
  BaseView = -> ProjItem008
  CoarseView = false
  CutSurfaceDisplay = 2
  Direction = (-1,2e-16,0)
  FileGeomPattern = <path>
  FileHatchPattern = <path>
  Focus = 100
  FuseBeforeCut = false
  HardHidden = false
  HatchScale = 1
  IsoCount = 0
  IsoHidden = false
  IsoVisible = false
  LockPosition = false
  NameGeomPattern = Diamond
  Perspective = false
  Rotation = 0
  Scale = 4
  ScaleType = 2
  SeamHidden = false
  SeamVisible = true
  SectionDirection = 2
  SectionNormal = (-1,2e-16,0)
  SectionOrigin = (30,21,-0.91)
  SmoothHidden = false
  SmoothVisible = true
  Source = -> [Cut007]
  X = 188.046
  XDirection = (2e-16,1,0)
  Y = 84.1822
FEATURE [TechDraw::DrawViewDimension] Dimension038
  AngleOverride = false
  Arbitrary = false
  ArbitraryTolerances = false
  EqualTolerance = true
  ExtensionAngle = 0
  FormatSpec = %.2w
  FormatSpecOverTolerance = %+.2w
  FormatSpecUnderTolerance = %+.2w
  Inverted = false
  LineAngle = 0
  LockPosition = false
  MeasureType = 1
  OverTolerance = 0
  References2D = -> [SectionView]
  Rotation = 0
  ScaleType = 0
  TheoreticalExact = false
  Type = 0
  UnderTolerance = 0
  X = -0.1308
  Y = 40.3604
FEATURE [TechDraw::DrawViewDimension] Dimension040
  AngleOverride = false
  Arbitrary = false
  ArbitraryTolerances = false
  EqualTolerance = true
  ExtensionAngle = 0
  FormatSpec = %.2w
  FormatSpecOverTolerance = %+.2w
  FormatSpecUnderTolerance = %+.2w
  Inverted = false
  LineAngle = 0
  LockPosition = false
  MeasureType = 1
  OverTolerance = 0
  References2D = -> [SectionView]
  Rotation = 0
  ScaleType = 0
  TheoreticalExact = false
  Type = 0
  UnderTolerance = 0
  X = -109.891
  Y = 21.16
FEATURE [TechDraw::DrawViewDimension] Dimension041
  AngleOverride = false
  Arbitrary = false
  ArbitraryTolerances = false
  EqualTolerance = true
  ExtensionAngle = 0
  FormatSpec = %.2w
  FormatSpecOverTolerance = %+.2w
  FormatSpecUnderTolerance = %+.2w
  Inverted = false
  LineAngle = 0
  LockPosition = false
  MeasureType = 1
  OverTolerance = 0
  References2D = -> [SectionView]
  Rotation = 0
  ScaleType = 0
  TheoreticalExact = false
  Type = 0
  UnderTolerance = 0
  X = -102.281
  Y = 21.8105
FEATURE [TechDraw::DrawViewDimension] Dimension042
  AngleOverride = false
  Arbitrary = false
  ArbitraryTolerances = false
  EqualTolerance = true
  ExtensionAngle = 0
  FormatSpec = %.2w
  FormatSpecOverTolerance = %+.2w
  FormatSpecUnderTolerance = %+.2w
  Inverted = false
  LineAngle = 0
  LockPosition = false
  MeasureType = 1
  OverTolerance = 0
  References2D = -> [SectionView]
  Rotation = 0
  ScaleType = 0
  TheoreticalExact = false
  Type = 0
  UnderTolerance = 0
  X = -36.8715
  Y = 3.63133
FEATURE [TechDraw::DrawViewDimension] Dimension043
  AngleOverride = false
  Arbitrary = false
  ArbitraryTolerances = false
  EqualTolerance = true
  ExtensionAngle = 0
  FormatSpec = %.2w
  FormatSpecOverTolerance = %+.2w
  FormatSpecUnderTolerance = %+.2w
  Inverted = false
  LineAngle = 0
  LockPosition = false
  MeasureType = 1
  OverTolerance = 0
  References2D = -> [SectionView]
  Rotation = 0
  ScaleType = 0
  TheoreticalExact = false
  Type = 0
  UnderTolerance = 0
  X = -49.3253
  Y = -4.92985
FEATURE [TechDraw::DrawViewDimension] Dimension044
  AngleOverride = false
  Arbitrary = false
  ArbitraryTolerances = false
  EqualTolerance = true
  ExtensionAngle = 0
  FormatSpec = %.2w
  FormatSpecOverTolerance = %+.2w
  FormatSpecUnderTolerance = %+.2w
  Inverted = false
  LineAngle = 0
  LockPosition = false
  MeasureType = 1
  OverTolerance = 0
  References2D = -> [SectionView]
  Rotation = 0
  ScaleType = 0
  TheoreticalExact = false
  Type = 0
  UnderTolerance = 0
  X = -74.7154
  Y = -18.2899
FEATURE [TechDraw::DrawViewDimension] Dimension045
  AngleOverride = false
  Arbitrary = false
  ArbitraryTolerances = false
  EqualTolerance = true
  ExtensionAngle = 0
  FormatSpec = %.2w
  FormatSpecOverTolerance = %+.2w
  FormatSpecUnderTolerance = %+.2w
  Inverted = false
  LineAngle = 0
  LockPosition = false
  MeasureType = 1
  OverTolerance = 0
  References2D = -> [SectionView]
  Rotation = 0
  ScaleType = 0
  TheoreticalExact = false
  Type = 0
  UnderTolerance = 0
  X = -74.363
  Y = -26.6033
FEATURE [TechDraw::DrawPage] Page002
  KeepUpdated = true
  NextBalloonIndex = 1
  ProjectionType = 0
  Template = -> Template002
  Views = -> [ProjGroup002,SectionView,Dimension038,Dimension040,Dimension041,Dimension042,Dimension043,Dimension044,Dimension045]
note: 2 file-system paths scrubbed to <path> (originals preserved in the JSON sidecar)
